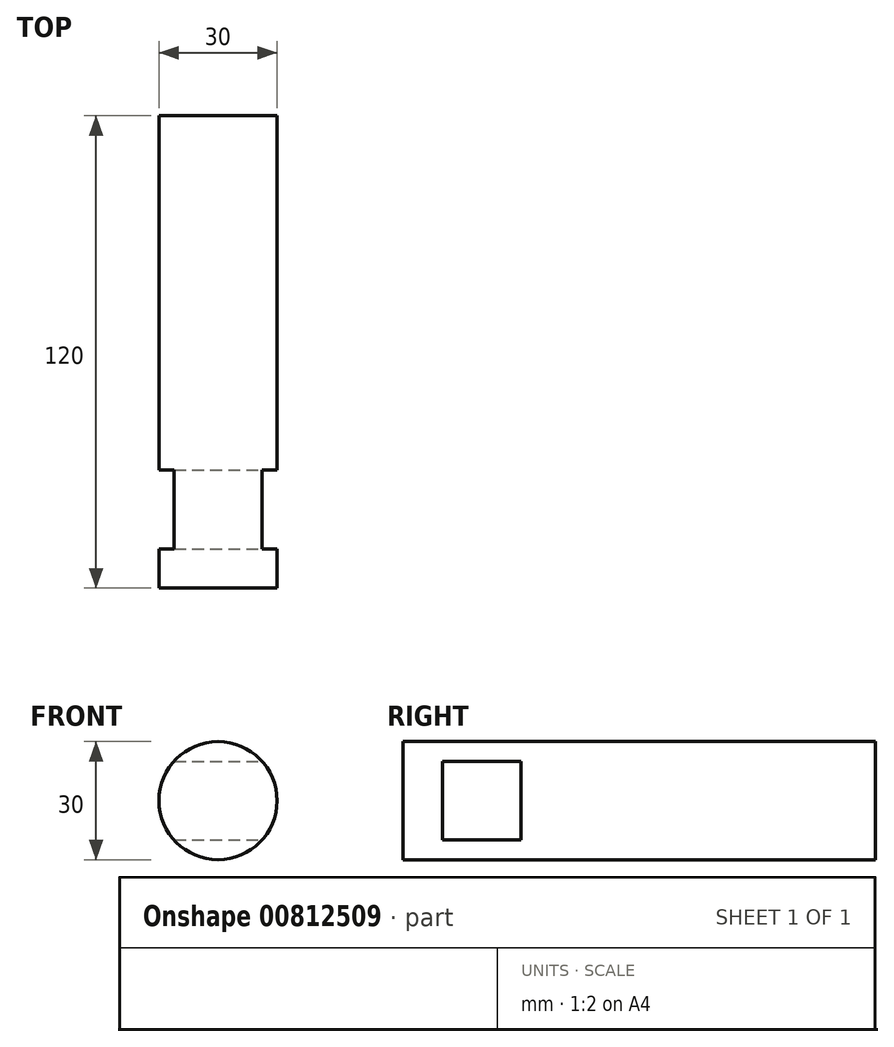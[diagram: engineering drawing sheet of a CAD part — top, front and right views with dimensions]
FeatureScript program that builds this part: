
annotation { "Feature Type Name" : "Feature", "Feature Type Description" : "" }
export const myFeature = defineFeature(function(context is Context, id is Id, definition is map)
    precondition{}
    {
        {
            var Q0;
            Q0=qCreatedBy(makeId("Front.planeOp"),FACE);
            var sketch = newSketch(context, id + "F0", { "sketchPlane" : qUnion([Q0])});
            skCircle(sketch, "E0", {"center": v(0, 0) * mm, "radius": 15 * mm});
            skSolve(sketch);
        }
        {
            var Q0;
            Q0 = qSketchRegion(id + "F0", true);
            extrude(context, id + "F1", {"entities" : qUnion([Q0]), "oppositeDirection" : true, "depth" : 120 * mm, "offsetDistance" : 25 * mm});
        }
        {
            var Q0;
            Q0=qCreatedBy(makeId("Right.planeOp"),FACE);
            var sketch = newSketch(context, id + "F2", { "sketchPlane" : qUnion([Q0])});
            skLineSegment(sketch, "E1.bottom", {"start": v(30, 10) * mm, "end": v(10, 10) * mm});
            skLineSegment(sketch, "E1.top", {"start": v(30, -10) * mm, "end": v(10, -10) * mm});
            skLineSegment(sketch, "E1.left", {"start": v(30, 10) * mm, "end": v(30, -10) * mm});
            skLineSegment(sketch, "E1.right", {"start": v(10, 10) * mm, "end": v(10, -10) * mm});
            skSolve(sketch);
        }
        {
            var Q0;
            Q0 = qSketchRegion(id + "F2", true);
            extrude(context, id + "F3", {"entities" : qUnion([Q0]), "operationType" : NewBodyOperationType.REMOVE, "endBound" : BoundingType.SYMMETRIC, "oppositeDirection" : true, "depth" : 62 * mm, "offsetDistance" : 25 * mm});
        }
    });
